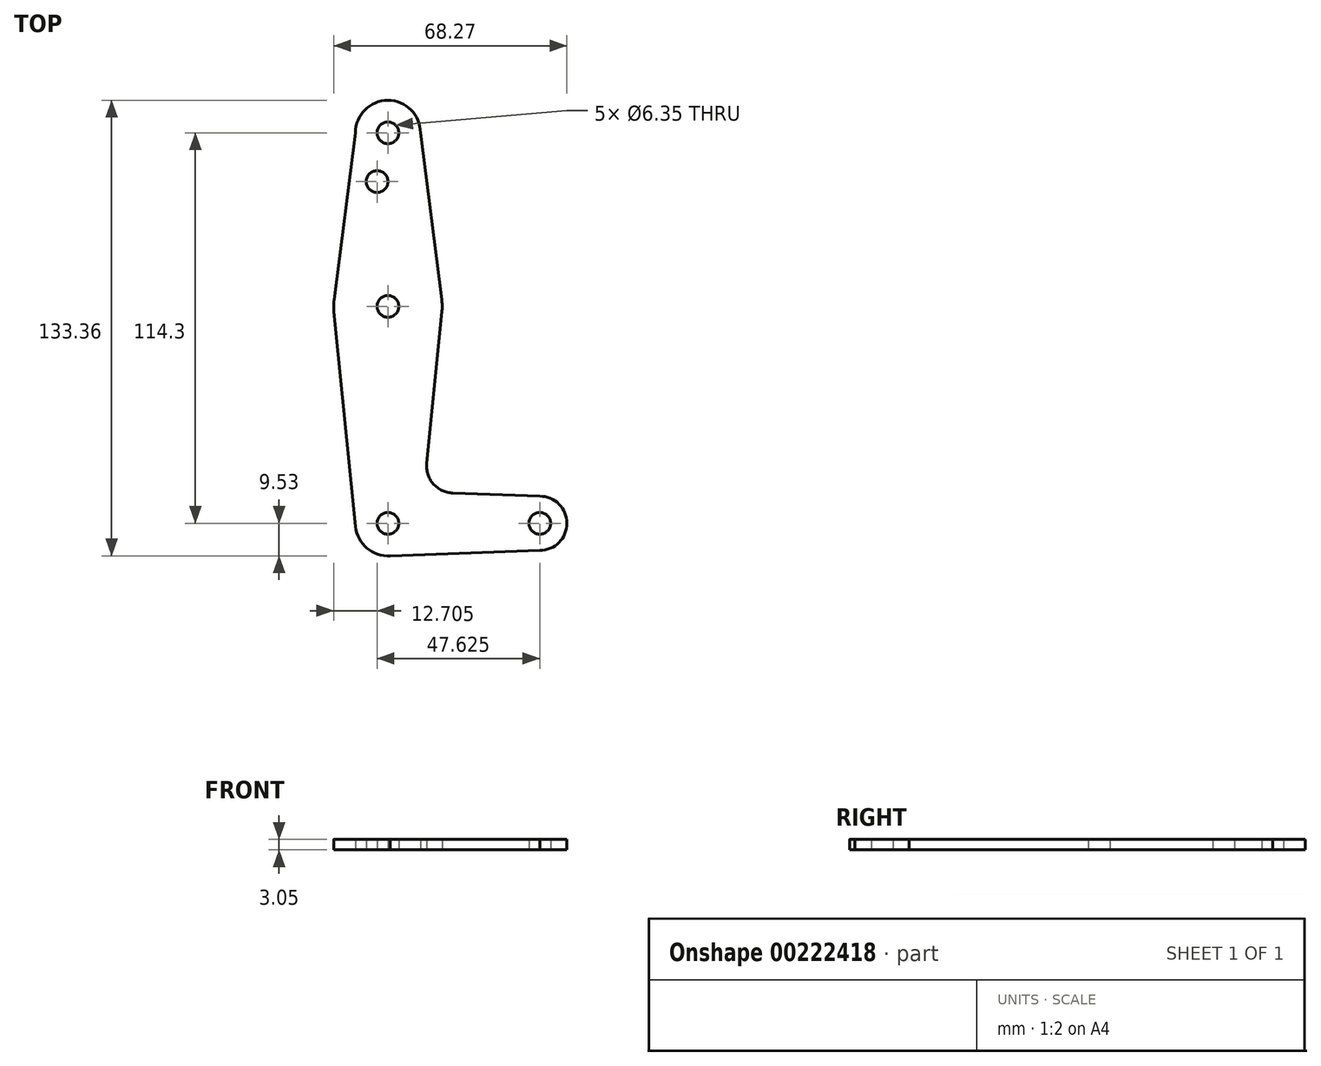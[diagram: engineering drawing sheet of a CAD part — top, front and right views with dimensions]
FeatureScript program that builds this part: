
annotation { "Feature Type Name" : "Feature", "Feature Type Description" : "" }
export const myFeature = defineFeature(function(context is Context, id is Id, definition is map)
    precondition{}
    {
        {
            var Q0;
            Q0=qCreatedBy(makeId("Top.planeOp"),FACE);
            var sketch = newSketch(context, id + "F0", { "sketchPlane" : qUnion([Q0])});
            skCircle(sketch, "E0", {"center": v(0, 0) * mm, "radius": 9.53 * mm});
            skCircle(sketch, "E1", {"center": v(0, 114.3) * mm, "radius": 9.53 * mm});
            skCircle(sketch, "E2", {"center": v(0, 63.5) * mm, "radius": 15.88 * mm});
            skCircle(sketch, "E3", {"center": v(44.45, 0) * mm, "radius": 7.94 * mm});
            skLineSegment(sketch, "E4", {"start": v(0, 114.3) * mm, "end": v(0, 0) * mm, "construction": true});
            skLineSegment(sketch, "E5", {"start": v(0, 0) * mm, "end": v(44.45, 0) * mm, "construction": true});
            skLineSegment(sketch, "E6", {"start": v(-9.52, 114.3) * mm, "end": v(-15.75, 65.5) * mm});
            skLineSegment(sketch, "E7", {"start": v(-15.8, 61.91) * mm, "end": v(-9.48, -0.95) * mm});
            skLineSegment(sketch, "E8.MirrorCS", {"start": v(15.8, 61.91) * mm, "end": v(11.34, 17.59) * mm});
            skLineSegment(sketch, "E9.MirrorCS", {"start": v(9.52, 114.3) * mm, "end": v(15.75, 65.5) * mm});
            skLineSegment(sketch, "E10", {"start": v(18.97, 8.85) * mm, "end": v(44.45, 7.94) * mm});
            skLineSegment(sketch, "E11.MirrorCS", {"start": v(0, -9.53) * mm, "end": v(44.45, -7.94) * mm});
            skCircle(sketch, "E12", {"center": v(0, 114.3) * mm, "radius": 3.18 * mm});
            skCircle(sketch, "E13", {"center": v(0, 63.5) * mm, "radius": 3.18 * mm});
            skCircle(sketch, "E14", {"center": v(0, 0) * mm, "radius": 3.18 * mm});
            skCircle(sketch, "E15", {"center": v(44.45, 0) * mm, "radius": 3.18 * mm});
            skCircle(sketch, "E16", {"center": v(-3.17, 100.03) * mm, "radius": 3.18 * mm});
            skPoint(sketch, "E17.newPointA", {"position": v(9.48, -0.95) * mm});
            skPoint(sketch, "E17.newPointB", {"position": v(0, 9.53) * mm});
            skArc(sketch, "E17.filletArc", {"start": v(11.34, 17.59) * mm, "mid": v(13.26, 11.57) * mm, "end": v(18.97, 8.85) * mm});
            skSolve(sketch);
        }
        {
            var Q0;
            Q0 = qSketchRegion(id + "F0", true);
            extrude(context, id + "F1", {"entities" : qUnion([Q0]), "depth" : 3.05 * mm});
        }
    });
